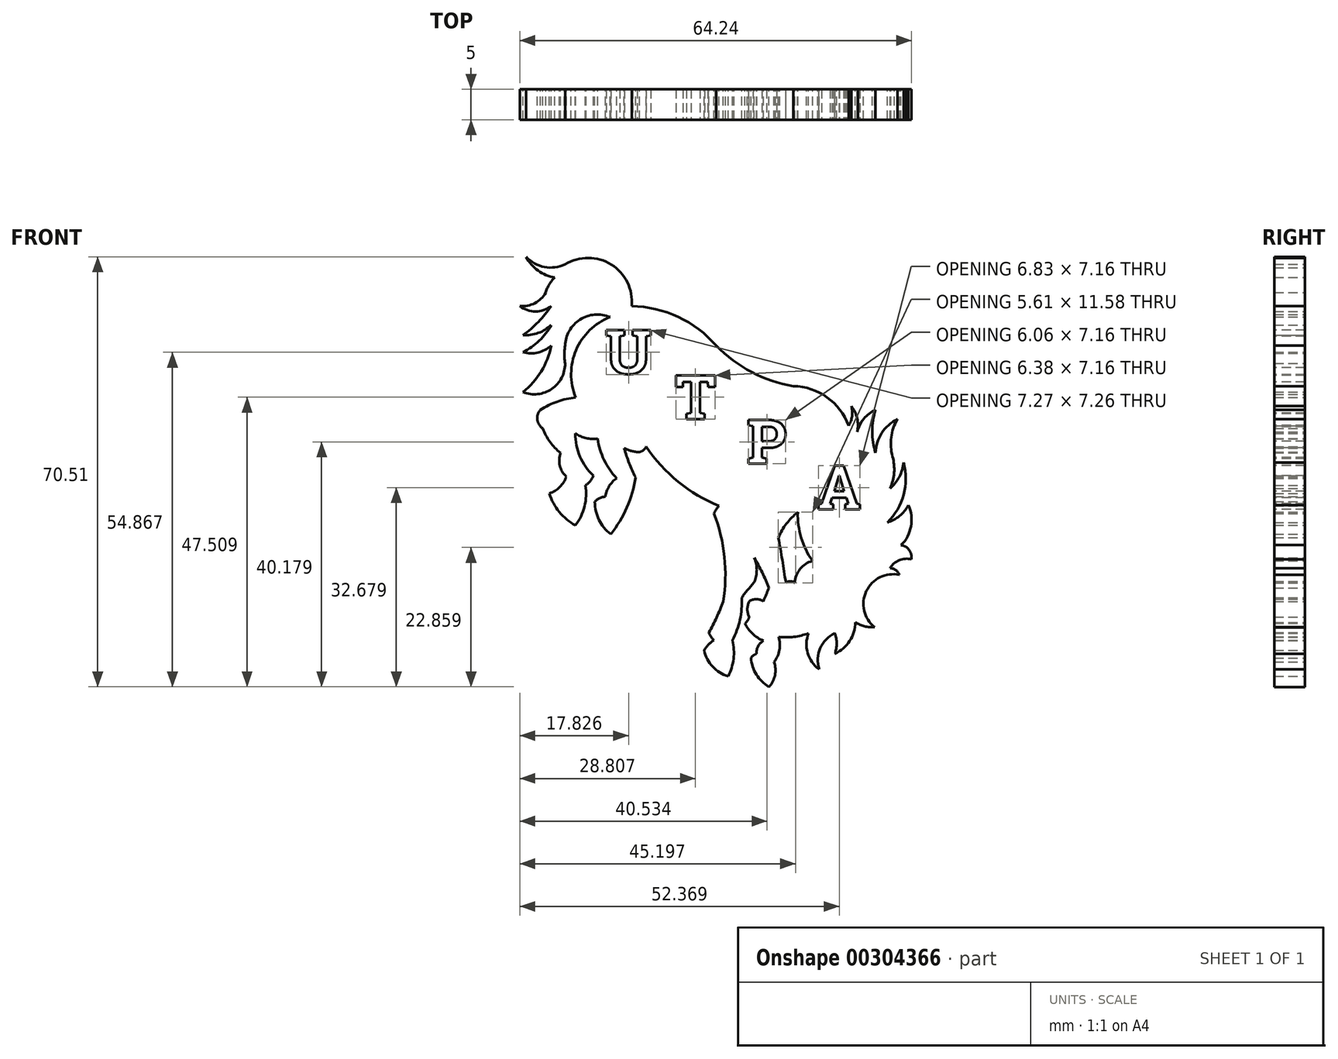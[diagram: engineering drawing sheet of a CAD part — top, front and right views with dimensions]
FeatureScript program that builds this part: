
annotation { "Feature Type Name" : "Feature", "Feature Type Description" : "" }
export const myFeature = defineFeature(function(context is Context, id is Id, definition is map)
    precondition{}
    {
        {
            var Q0;
            Q0=qCreatedBy(makeId("Front.planeOp"),FACE);
            var sketch = newSketch(context, id + "F0", { "sketchPlane" : qUnion([Q0])});
            skArc(sketch, "E0", {"start": v(-25.13, 23.44) * mm, "mid": v(-30.7, 18.04) * mm, "end": v(-30.76, 10.27) * mm});
            skArc(sketch, "E1", {"start": v(-30.76, 10.27) * mm, "mid": v(-33.78, 9.59) * mm, "end": v(-36.56, 8.24) * mm});
            skArc(sketch, "E2", {"start": v(-36.56, 8.24) * mm, "mid": v(-37.05, 6.61) * mm, "end": v(-36.16, 5.17) * mm});
            skArc(sketch, "E3", {"start": v(-36.16, 5.17) * mm, "mid": v(-34.97, 2.97) * mm, "end": v(-33.26, 1.16) * mm});
            skArc(sketch, "E4", {"start": v(-33.26, 1.16) * mm, "mid": v(-33.36, -0.92) * mm, "end": v(-32.33, -2.72) * mm});
            skArc(sketch, "E5", {"start": v(-25.13, 23.44) * mm, "mid": v(-30.05, 23.03) * mm, "end": v(-32.5, 18.74) * mm});
            skArc(sketch, "E6", {"start": v(-32.5, 18.74) * mm, "mid": v(-32.62, 17.3) * mm, "end": v(-32.5, 15.84) * mm});
            skArc(sketch, "E7", {"start": v(-39.4, 11.14) * mm, "mid": v(-34.7, 11.66) * mm, "end": v(-32.5, 15.84) * mm});
            skArc(sketch, "E8", {"start": v(-39.4, 11.14) * mm, "mid": v(-36.42, 14.54) * mm, "end": v(-34.76, 18.74) * mm});
            skArc(sketch, "E9", {"start": v(-39.4, 17.7) * mm, "mid": v(-36.95, 17.63) * mm, "end": v(-34.76, 18.74) * mm});
            skArc(sketch, "E10", {"start": v(-39.4, 17.7) * mm, "mid": v(-36.74, 19.58) * mm, "end": v(-34.76, 22.17) * mm});
            skArc(sketch, "E11", {"start": v(-39.4, 20.48) * mm, "mid": v(-36.9, 20.84) * mm, "end": v(-34.76, 22.17) * mm});
            skArc(sketch, "E12", {"start": v(-39.4, 20.48) * mm, "mid": v(-36.88, 22.66) * mm, "end": v(-34.76, 25.24) * mm});
            skArc(sketch, "E13", {"start": v(-39.93, 25.24) * mm, "mid": v(-37.35, 24.37) * mm, "end": v(-34.76, 25.24) * mm});
            skArc(sketch, "E14", {"start": v(-39.93, 25.24) * mm, "mid": v(-37.49, 25.72) * mm, "end": v(-35.7, 27.45) * mm});
            skArc(sketch, "E15", {"start": v(-34.18, 29.94) * mm, "mid": v(-35.11, 28.8) * mm, "end": v(-35.7, 27.45) * mm});
            skArc(sketch, "E16", {"start": v(-38.88, 33.3) * mm, "mid": v(-36.93, 31.07) * mm, "end": v(-34.18, 29.94) * mm});
            skArc(sketch, "E17", {"start": v(-38.88, 33.3) * mm, "mid": v(-35.9, 31.66) * mm, "end": v(-32.5, 32.09) * mm});
            skArc(sketch, "E18", {"start": v(-21.6, 25.24) * mm, "mid": v(-24.93, 32.04) * mm, "end": v(-32.5, 32.09) * mm});
            skArc(sketch, "E19", {"start": v(-7.73, 18.74) * mm, "mid": v(-13.96, 23.48) * mm, "end": v(-21.6, 25.24) * mm});
            skArc(sketch, "E20", {"start": v(-7.73, 18.74) * mm, "mid": v(-1.93, 14.43) * mm, "end": v(4.92, 12.13) * mm});
            skArc(sketch, "E21", {"start": v(13.98, 5.63) * mm, "mid": v(10.46, 10.29) * mm, "end": v(4.92, 12.13) * mm});
            skArc(sketch, "E22", {"start": v(13.98, 5.63) * mm, "mid": v(14.54, 7.2) * mm, "end": v(14.42, 8.85) * mm});
            skArc(sketch, "E23", {"start": v(15.36, 4.5) * mm, "mid": v(15.39, 6.78) * mm, "end": v(14.42, 8.85) * mm});
            skArc(sketch, "E24", {"start": v(18.4, 8.24) * mm, "mid": v(16.43, 6.73) * mm, "end": v(15.36, 4.5) * mm});
            skArc(sketch, "E25", {"start": v(18.4, 8.24) * mm, "mid": v(17.85, 4.7) * mm, "end": v(18.4, 1.16) * mm});
            skArc(sketch, "E26", {"start": v(21.97, 6.68) * mm, "mid": v(19.4, 4.42) * mm, "end": v(18.4, 1.16) * mm});
            skArc(sketch, "E27", {"start": v(21.97, 6.68) * mm, "mid": v(20.96, 3.7) * mm, "end": v(21.19, 0.56) * mm});
            skArc(sketch, "E28", {"start": v(20.78, -4.65) * mm, "mid": v(21.44, -2.08) * mm, "end": v(21.19, 0.56) * mm});
            skArc(sketch, "E29", {"start": v(20.78, -4.65) * mm, "mid": v(22.3, -2.75) * mm, "end": v(23, -0.42) * mm});
            skArc(sketch, "E30", {"start": v(20.32, -10.23) * mm, "mid": v(23.01, -5.7) * mm, "end": v(23, -0.42) * mm});
            skArc(sketch, "E31", {"start": v(20.32, -10.23) * mm, "mid": v(22.34, -9.16) * mm, "end": v(23.77, -7.4) * mm});
            skArc(sketch, "E32", {"start": v(22.59, -13.95) * mm, "mid": v(24.22, -10.86) * mm, "end": v(23.77, -7.4) * mm});
            skArc(sketch, "E33", {"start": v(24.27, -16.27) * mm, "mid": v(23.92, -14.76) * mm, "end": v(22.59, -13.95) * mm});
            skArc(sketch, "E34", {"start": v(24.27, -16.27) * mm, "mid": v(22.29, -16.42) * mm, "end": v(20.79, -17.72) * mm});
            skArc(sketch, "E35", {"start": v(22.3, -18.83) * mm, "mid": v(21.71, -18.04) * mm, "end": v(20.79, -17.72) * mm});
            skArc(sketch, "E36", {"start": v(22.3, -18.83) * mm, "mid": v(16.88, -21.52) * mm, "end": v(18.23, -27.41) * mm});
            skArc(sketch, "E37", {"start": v(15.1, -26.6) * mm, "mid": v(16.6, -27.26) * mm, "end": v(18.23, -27.41) * mm});
            skArc(sketch, "E38", {"start": v(11.74, -31.76) * mm, "mid": v(14.15, -29.66) * mm, "end": v(15.1, -26.6) * mm});
            skArc(sketch, "E39", {"start": v(11.74, -31.76) * mm, "mid": v(12.02, -30.08) * mm, "end": v(11.74, -28.4) * mm});
            skArc(sketch, "E40", {"start": v(11.74, -28.4) * mm, "mid": v(9.32, -30.86) * mm, "end": v(9.14, -34.3) * mm});
            skArc(sketch, "E41", {"start": v(7.41, -28.4) * mm, "mid": v(7.27, -31.65) * mm, "end": v(9.14, -34.3) * mm});
            skArc(sketch, "E42", {"start": v(2.51, -29) * mm, "mid": v(5, -29) * mm, "end": v(7.41, -28.4) * mm});
            skArc(sketch, "E43", {"start": v(1.76, -33.13) * mm, "mid": v(2.65, -31.16) * mm, "end": v(2.51, -29) * mm});
            skArc(sketch, "E44", {"start": v(0.93, -37.2) * mm, "mid": v(1.9, -35.28) * mm, "end": v(1.76, -33.13) * mm});
            skArc(sketch, "E45", {"start": v(-2.03, -32.44) * mm, "mid": v(-1.13, -35.18) * mm, "end": v(0.93, -37.2) * mm});
            skArc(sketch, "E46", {"start": v(-1.14, -31.76) * mm, "mid": v(-1.64, -32.04) * mm, "end": v(-2.03, -32.44) * mm});
            skArc(sketch, "E47", {"start": v(0, -29.61) * mm, "mid": v(-0.85, -30.54) * mm, "end": v(-1.14, -31.76) * mm});
            skArc(sketch, "E48", {"start": v(-3, -26.79) * mm, "mid": v(-1.78, -28.5) * mm, "end": v(0, -29.61) * mm});
            skArc(sketch, "E49", {"start": v(-3, -26.79) * mm, "mid": v(-2.58, -26.32) * mm, "end": v(-2.32, -25.75) * mm});
            skArc(sketch, "E50", {"start": v(-2.32, -23.2) * mm, "mid": v(-2.62, -24.47) * mm, "end": v(-2.32, -25.75) * mm});
            skArc(sketch, "E51", {"start": v(0, -23.2) * mm, "mid": v(-1.16, -22.81) * mm, "end": v(-2.32, -23.2) * mm});
            skArc(sketch, "E52", {"start": v(0.93, -20.99) * mm, "mid": v(0.45, -22.09) * mm, "end": v(0, -23.2) * mm});
            skArc(sketch, "E53", {"start": v(0.93, -20.99) * mm, "mid": v(-0.19, -18.46) * mm, "end": v(-1.49, -16.02) * mm});
            skArc(sketch, "E54", {"start": v(-1.49, -20.02) * mm, "mid": v(-1.09, -18.02) * mm, "end": v(-1.49, -16.02) * mm});
            skArc(sketch, "E55", {"start": v(-1.49, -20.02) * mm, "mid": v(-2.55, -21.28) * mm, "end": v(-3.56, -22.58) * mm});
            skArc(sketch, "E56", {"start": v(-5.08, -29.55) * mm, "mid": v(-3.83, -26.17) * mm, "end": v(-3.56, -22.58) * mm});
            skArc(sketch, "E57", {"start": v(-5.77, -35.48) * mm, "mid": v(-4.88, -32.58) * mm, "end": v(-5.08, -29.55) * mm});
            skArc(sketch, "E58", {"start": v(-9.7, -31.2) * mm, "mid": v(-8.32, -33.88) * mm, "end": v(-5.77, -35.48) * mm});
            skArc(sketch, "E59", {"start": v(-8.11, -29.55) * mm, "mid": v(-9, -30.28) * mm, "end": v(-9.7, -31.2) * mm});
            skArc(sketch, "E60", {"start": v(-8.94, -28.3) * mm, "mid": v(-8.6, -28.97) * mm, "end": v(-8.11, -29.55) * mm});
            skArc(sketch, "E61", {"start": v(-8.94, -28.3) * mm, "mid": v(-7.67, -25.8) * mm, "end": v(-6.6, -23.2) * mm});
            skArc(sketch, "E62", {"start": v(-6.6, -23.2) * mm, "mid": v(-6.38, -15.88) * mm, "end": v(-8.11, -8.78) * mm});
            skArc(sketch, "E63", {"start": v(-7.28, -7.53) * mm, "mid": v(-7.75, -8.12) * mm, "end": v(-8.11, -8.78) * mm});
            skArc(sketch, "E64", {"start": v(-19.22, 2.2) * mm, "mid": v(-13.97, -3.55) * mm, "end": v(-7.28, -7.53) * mm});
            skArc(sketch, "E65", {"start": v(-20.33, 1.3) * mm, "mid": v(-19.67, 1.63) * mm, "end": v(-19.22, 2.2) * mm});
            skArc(sketch, "E66", {"start": v(-22.8, 1.92) * mm, "mid": v(-21.6, 1.48) * mm, "end": v(-20.33, 1.3) * mm});
            skArc(sketch, "E67", {"start": v(-22.8, 1.92) * mm, "mid": v(-22, -0.5) * mm, "end": v(-20.95, -2.84) * mm});
            skArc(sketch, "E68", {"start": v(-25.02, -12.16) * mm, "mid": v(-22.37, -7.77) * mm, "end": v(-20.95, -2.84) * mm});
            skArc(sketch, "E69", {"start": v(-27.64, -6.84) * mm, "mid": v(-26.95, -9.8) * mm, "end": v(-25.02, -12.16) * mm});
            skArc(sketch, "E70", {"start": v(-25.91, -6.02) * mm, "mid": v(-26.86, -6.25) * mm, "end": v(-27.64, -6.84) * mm});
            skArc(sketch, "E71", {"start": v(-24.05, -2.98) * mm, "mid": v(-25.3, -4.3) * mm, "end": v(-25.91, -6.02) * mm});
            skArc(sketch, "E72", {"start": v(-27.16, 3.5) * mm, "mid": v(-26.11, 0.02) * mm, "end": v(-24.05, -2.98) * mm});
            skArc(sketch, "E73", {"start": v(-30.81, 4.36) * mm, "mid": v(-29.06, 3.59) * mm, "end": v(-27.16, 3.5) * mm});
            skArc(sketch, "E74", {"start": v(-30.81, 4.36) * mm, "mid": v(-30.07, 0.58) * mm, "end": v(-27.85, -2.57) * mm});
            skArc(sketch, "E75", {"start": v(-29.16, -4.15) * mm, "mid": v(-28.38, -3.46) * mm, "end": v(-27.85, -2.57) * mm});
            skArc(sketch, "E76", {"start": v(-30.81, -10.7) * mm, "mid": v(-29.32, -7.6) * mm, "end": v(-29.16, -4.15) * mm});
            skArc(sketch, "E77", {"start": v(-35.1, -5.46) * mm, "mid": v(-33.46, -8.5) * mm, "end": v(-30.81, -10.7) * mm});
            skArc(sketch, "E78", {"start": v(-35.1, -5.46) * mm, "mid": v(-33.38, -4.43) * mm, "end": v(-32.33, -2.72) * mm});
            skArc(sketch, "E79", {"start": v(5.64, -8.55) * mm, "mid": v(3.8, -10.43) * mm, "end": v(2.46, -12.71) * mm});
            skArc(sketch, "E80", {"start": v(3.69, -20.13) * mm, "mid": v(3.1, -16.41) * mm, "end": v(2.46, -12.71) * mm});
            skArc(sketch, "E81", {"start": v(5.15, -20.13) * mm, "mid": v(4.42, -19.88) * mm, "end": v(3.69, -20.13) * mm});
            skArc(sketch, "E82", {"start": v(8.07, -16.54) * mm, "mid": v(6.02, -17.86) * mm, "end": v(5.15, -20.13) * mm});
            skArc(sketch, "E83", {"start": v(5.64, -8.55) * mm, "mid": v(6.2, -12.74) * mm, "end": v(8.07, -16.54) * mm});
            skSolve(sketch);
        }
        {
            var Q0;
            Q0 = qSketchRegion(id + "F0", true);
            extrude(context, id + "F1", {"entities" : qUnion([Q0]), "depth" : 5 * mm});
        }
        {
            var Q0;
            Q0=makeQuery(id+"F1.opExtrude","CAP_FACE",FACE,{"disambiguationData":[OSD([sQuery(id+"F0.wireOp",EDGE,"E0"),sQuery(id+"F0.wireOp",EDGE,"E1"),sQuery(id+"F0.wireOp",EDGE,"E2"),sQuery(id+"F0.wireOp",EDGE,"E3"),sQuery(id+"F0.wireOp",EDGE,"E4"),sQuery(id+"F0.wireOp",EDGE,"E5"),sQuery(id+"F0.wireOp",EDGE,"E6"),sQuery(id+"F0.wireOp",EDGE,"E7"),sQuery(id+"F0.wireOp",EDGE,"E8"),sQuery(id+"F0.wireOp",EDGE,"E9"),sQuery(id+"F0.wireOp",EDGE,"E10"),sQuery(id+"F0.wireOp",EDGE,"E11"),sQuery(id+"F0.wireOp",EDGE,"E12"),sQuery(id+"F0.wireOp",EDGE,"E13"),sQuery(id+"F0.wireOp",EDGE,"E14"),sQuery(id+"F0.wireOp",EDGE,"E15"),sQuery(id+"F0.wireOp",EDGE,"E16"),sQuery(id+"F0.wireOp",EDGE,"E17"),sQuery(id+"F0.wireOp",EDGE,"E18"),sQuery(id+"F0.wireOp",EDGE,"E19"),sQuery(id+"F0.wireOp",EDGE,"E20"),sQuery(id+"F0.wireOp",EDGE,"E21"),sQuery(id+"F0.wireOp",EDGE,"E22"),sQuery(id+"F0.wireOp",EDGE,"E23"),sQuery(id+"F0.wireOp",EDGE,"E24"),sQuery(id+"F0.wireOp",EDGE,"E25"),sQuery(id+"F0.wireOp",EDGE,"E26"),sQuery(id+"F0.wireOp",EDGE,"E27"),sQuery(id+"F0.wireOp",EDGE,"E28"),sQuery(id+"F0.wireOp",EDGE,"E29"),sQuery(id+"F0.wireOp",EDGE,"E30"),sQuery(id+"F0.wireOp",EDGE,"E31"),sQuery(id+"F0.wireOp",EDGE,"E32"),sQuery(id+"F0.wireOp",EDGE,"E33"),sQuery(id+"F0.wireOp",EDGE,"E34"),sQuery(id+"F0.wireOp",EDGE,"E35"),sQuery(id+"F0.wireOp",EDGE,"E36"),sQuery(id+"F0.wireOp",EDGE,"E37"),sQuery(id+"F0.wireOp",EDGE,"E38"),sQuery(id+"F0.wireOp",EDGE,"E39"),sQuery(id+"F0.wireOp",EDGE,"E40"),sQuery(id+"F0.wireOp",EDGE,"E41"),sQuery(id+"F0.wireOp",EDGE,"E42"),sQuery(id+"F0.wireOp",EDGE,"E43"),sQuery(id+"F0.wireOp",EDGE,"E44"),sQuery(id+"F0.wireOp",EDGE,"E45"),sQuery(id+"F0.wireOp",EDGE,"E46"),sQuery(id+"F0.wireOp",EDGE,"E47"),sQuery(id+"F0.wireOp",EDGE,"E48"),sQuery(id+"F0.wireOp",EDGE,"E49"),sQuery(id+"F0.wireOp",EDGE,"E50"),sQuery(id+"F0.wireOp",EDGE,"E51"),sQuery(id+"F0.wireOp",EDGE,"E52"),sQuery(id+"F0.wireOp",EDGE,"E53"),sQuery(id+"F0.wireOp",EDGE,"E54"),sQuery(id+"F0.wireOp",EDGE,"E55"),sQuery(id+"F0.wireOp",EDGE,"E56"),sQuery(id+"F0.wireOp",EDGE,"E57"),sQuery(id+"F0.wireOp",EDGE,"E58"),sQuery(id+"F0.wireOp",EDGE,"E59"),sQuery(id+"F0.wireOp",EDGE,"E60"),sQuery(id+"F0.wireOp",EDGE,"E61"),sQuery(id+"F0.wireOp",EDGE,"E62"),sQuery(id+"F0.wireOp",EDGE,"E63"),sQuery(id+"F0.wireOp",EDGE,"E64"),sQuery(id+"F0.wireOp",EDGE,"E65"),sQuery(id+"F0.wireOp",EDGE,"E66"),sQuery(id+"F0.wireOp",EDGE,"E67"),sQuery(id+"F0.wireOp",EDGE,"E68"),sQuery(id+"F0.wireOp",EDGE,"E69"),sQuery(id+"F0.wireOp",EDGE,"E70"),sQuery(id+"F0.wireOp",EDGE,"E71"),sQuery(id+"F0.wireOp",EDGE,"E72"),sQuery(id+"F0.wireOp",EDGE,"E73"),sQuery(id+"F0.wireOp",EDGE,"E74"),sQuery(id+"F0.wireOp",EDGE,"E75"),sQuery(id+"F0.wireOp",EDGE,"E76"),sQuery(id+"F0.wireOp",EDGE,"E77"),sQuery(id+"F0.wireOp",EDGE,"E78"),sQuery(id+"F0.wireOp",EDGE,"E79"),sQuery(id+"F0.wireOp",EDGE,"E80"),sQuery(id+"F0.wireOp",EDGE,"E81"),sQuery(id+"F0.wireOp",EDGE,"E82"),sQuery(id+"F0.wireOp",EDGE,"E83")])],"isStart":false});
            var sketch = newSketch(context, id + "F2", { "sketchPlane" : qUnion([Q0])});
            skText(sketch, "E84", { "text": "P", "fontName": "RobotoSlab-Bold.ttf"});
            skText(sketch, "E85", { "text": "U", "fontName": "RobotoSlab-Bold.ttf"});
            skText(sketch, "E86", { "text": "T", "fontName": "RobotoSlab-Bold.ttf"});
            skText(sketch, "E87", { "text": "A", "fontName": "RobotoSlab-Bold.ttf"});
            const initialGuessF2  = {"E84": [-0.0027, -0.0006, 1, 0, 0.00725], "E85": [-0.02593, 0.01414, 1, 0, 0.00725], "E86": [-0.01451, 0.00673, 1, 0, 0.00725], "E87": [0.00882, -0.0081, 1, 0, 0.00725]};
            skSetInitialGuess(sketch, initialGuessF2);
            skSolve(sketch);
        }
        {
            var Q0;
            Q0 = qSketchRegion(id + "F2", true);
            extrude(context, id + "F3", {"entities" : qUnion([Q0]), "operationType" : NewBodyOperationType.REMOVE, "oppositeDirection" : true, "depth" : 5 * mm});
        }
    });
